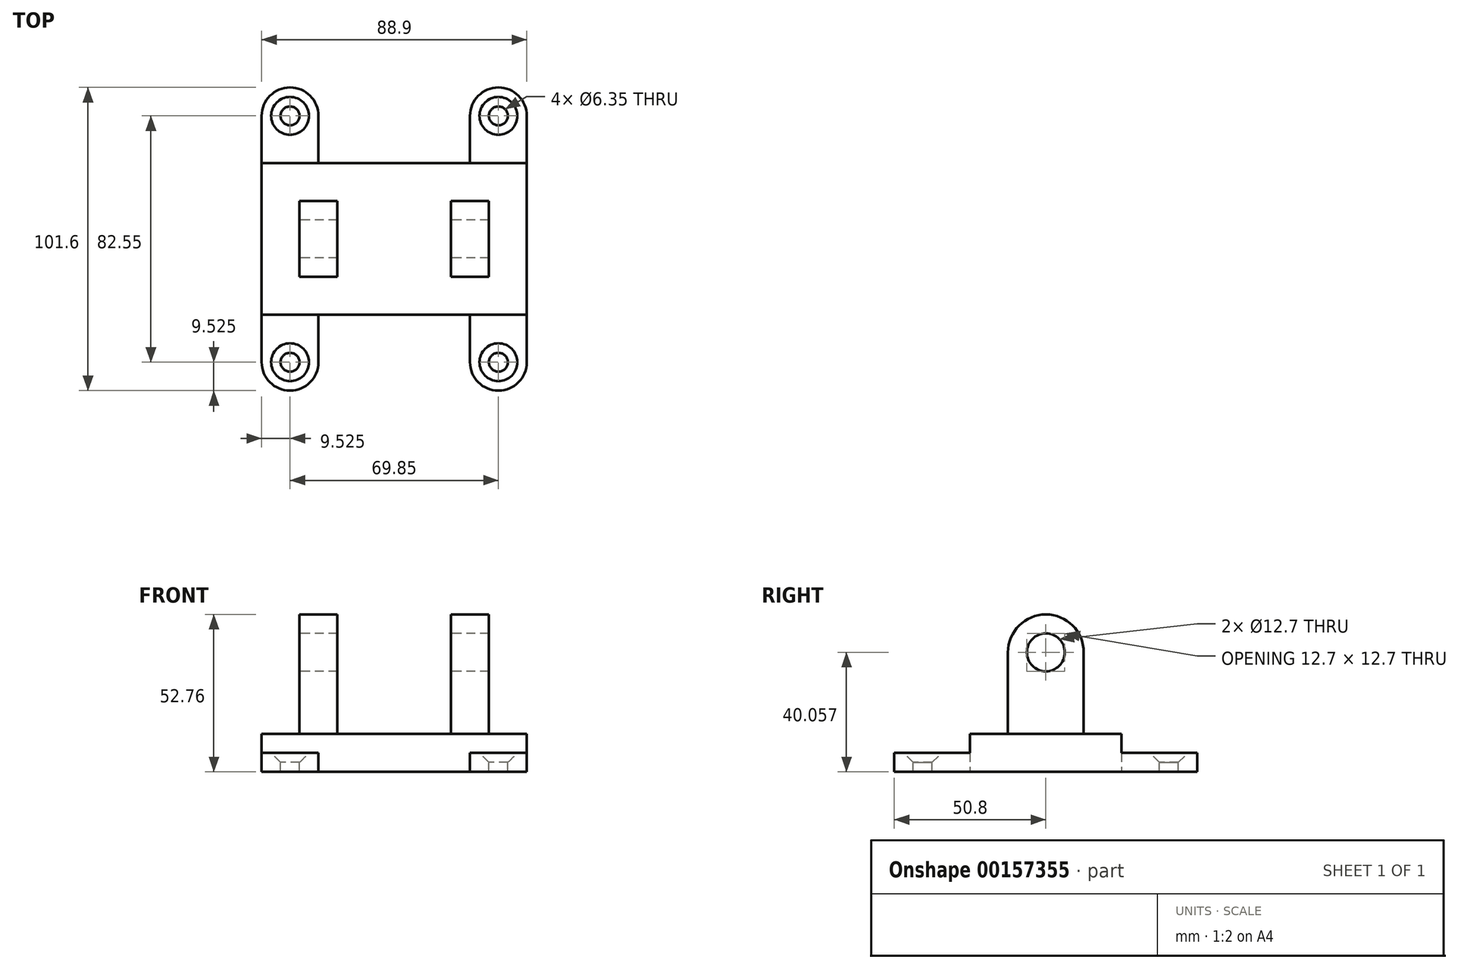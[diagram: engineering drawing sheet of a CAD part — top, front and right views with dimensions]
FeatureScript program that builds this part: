
annotation { "Feature Type Name" : "Feature", "Feature Type Description" : "" }
export const myFeature = defineFeature(function(context is Context, id is Id, definition is map)
    precondition{}
    {
        {
            var Q0;
            Q0=qCreatedBy(makeId("Front.planeOp"),FACE);
            var sketch = newSketch(context, id + "F0", { "sketchPlane" : qUnion([Q0])});
            skLineSegment(sketch, "E0.bottom", {"start": v(0, 0) * mm, "end": v(88.9, 0) * mm});
            skLineSegment(sketch, "E0.top", {"start": v(0, 12.7) * mm, "end": v(88.9, 12.7) * mm});
            skLineSegment(sketch, "E0.left", {"start": v(0, 0) * mm, "end": v(0, 12.7) * mm});
            skLineSegment(sketch, "E0.right", {"start": v(88.9, 0) * mm, "end": v(88.9, 12.7) * mm});
            skSolve(sketch);
        }
        {
            var Q0;
            Q0 = qSketchRegion(id + "F0", true);
            extrude(context, id + "F1", {"entities" : qUnion([Q0]), "depth" : 50.8 * mm});
        }
        {
            var Q0;
            Q0=qCreatedBy(makeId("Top.planeOp"),FACE);
            var sketch = newSketch(context, id + "F2", { "sketchPlane" : qUnion([Q0])});
            skLineSegment(sketch, "E1", {"start": v(0, 0) * mm, "end": v(0, 15.88) * mm});
            skLineSegment(sketch, "E2", {"start": v(0, 15.88) * mm, "end": v(19.05, 15.88) * mm});
            skLineSegment(sketch, "E3", {"start": v(19.05, 15.88) * mm, "end": v(19.05, 0) * mm});
            skLineSegment(sketch, "E4", {"start": v(19.05, 0) * mm, "end": v(69.85, 0) * mm});
            skLineSegment(sketch, "E5", {"start": v(69.85, 0) * mm, "end": v(69.85, 15.88) * mm});
            skLineSegment(sketch, "E6", {"start": v(69.85, 15.88) * mm, "end": v(88.9, 15.88) * mm});
            skLineSegment(sketch, "E7", {"start": v(88.9, 15.88) * mm, "end": v(88.9, 0) * mm});
            skLineSegment(sketch, "E8", {"start": v(0, 0) * mm, "end": v(0, -66.67) * mm});
            skLineSegment(sketch, "E9", {"start": v(0, -66.67) * mm, "end": v(19.05, -66.67) * mm});
            skLineSegment(sketch, "E10", {"start": v(19.05, -66.67) * mm, "end": v(19.05, -50.8) * mm});
            skLineSegment(sketch, "E11", {"start": v(19.05, -50.8) * mm, "end": v(69.85, -50.8) * mm});
            skLineSegment(sketch, "E12", {"start": v(69.85, -50.8) * mm, "end": v(69.85, -66.67) * mm});
            skLineSegment(sketch, "E13", {"start": v(69.85, -66.67) * mm, "end": v(88.9, -66.67) * mm});
            skLineSegment(sketch, "E14", {"start": v(88.9, -66.67) * mm, "end": v(88.9, -50.8) * mm});
            skArc(sketch, "E15", {"start": v(19.05, 15.88) * mm, "mid": v(9.53, 25.4) * mm, "end": v(0, 15.88) * mm});
            skArc(sketch, "E16", {"start": v(88.9, 15.88) * mm, "mid": v(79.38, 25.4) * mm, "end": v(69.85, 15.88) * mm});
            skArc(sketch, "E17", {"start": v(0, -66.67) * mm, "mid": v(9.53, -76.2) * mm, "end": v(19.05, -66.67) * mm});
            skArc(sketch, "E18", {"start": v(69.85, -66.67) * mm, "mid": v(79.38, -76.2) * mm, "end": v(88.9, -66.67) * mm});
            skLineSegment(sketch, "E19", {"start": v(0, -50.8) * mm, "end": v(19.05, -50.8) * mm});
            skLineSegment(sketch, "E20", {"start": v(69.85, -50.8) * mm, "end": v(88.9, -50.8) * mm});
            skLineSegment(sketch, "E21", {"start": v(69.85, 0) * mm, "end": v(88.9, 0) * mm});
            skLineSegment(sketch, "E22", {"start": v(19.05, 0) * mm, "end": v(0, 0) * mm});
            skCircle(sketch, "E23", {"center": v(79.38, 15.87) * mm, "radius": 3.18 * mm, "construction": true});
            skCircle(sketch, "E24", {"center": v(79.38, -66.67) * mm, "radius": 3.18 * mm, "construction": true});
            skCircle(sketch, "E25", {"center": v(9.53, -66.67) * mm, "radius": 3.18 * mm, "construction": true});
            skCircle(sketch, "E26", {"center": v(9.53, 15.88) * mm, "radius": 3.18 * mm, "construction": true});
            skSolve(sketch);
        }
        {
            var Q0;
            Q0 = qSketchRegion(id + "F2", true);
            extrude(context, id + "F3", {"entities" : qUnion([Q0]), "operationType" : NewBodyOperationType.ADD, "depth" : 6.35 * mm});
        }
        {
            var Q0;
            Q0=qCreatedBy(makeId("Right.planeOp"),FACE);
            var sketch = newSketch(context, id + "F4", { "sketchPlane" : qUnion([Q0])});
            skLineSegment(sketch, "E27.bottom", {"start": v(0, 0) * mm, "end": v(-50.8, 0) * mm});
            skLineSegment(sketch, "E27.top", {"start": v(0, 12.57) * mm, "end": v(-50.8, 12.57) * mm});
            skLineSegment(sketch, "E27.left", {"start": v(0, 0) * mm, "end": v(0, 12.57) * mm});
            skLineSegment(sketch, "E27.right", {"start": v(-50.8, 0) * mm, "end": v(-50.8, 12.57) * mm});
            skLineSegment(sketch, "E28", {"start": v(-38.1, 12.57) * mm, "end": v(-38.1, 40.06) * mm});
            skLineSegment(sketch, "E29", {"start": v(-38.1, 40.06) * mm, "end": v(-12.7, 40.06) * mm, "construction": true});
            skLineSegment(sketch, "E30", {"start": v(-12.7, 40.06) * mm, "end": v(-12.7, 12.57) * mm});
            skArc(sketch, "E31", {"start": v(-12.7, 40.06) * mm, "mid": v(-25.4, 52.76) * mm, "end": v(-38.1, 40.06) * mm});
            skCircle(sketch, "E32", {"center": v(-25.4, 40.06) * mm, "radius": 6.35 * mm});
            skSolve(sketch);
        }
        {
            var Q0;
            Q0 = qSketchRegion(id + "F4", true);
            extrude(context, id + "F5", {"entities" : qUnion([Q0]), "operationType" : NewBodyOperationType.ADD, "depth" : 76.2 * mm, "hasSecondDirection" : true, "secondDirectionOppositeDirection" : false, "secondDirectionDepth" : 12.7 * mm});
        }
        {
            var Q0;
            Q0=qCreatedBy(makeId("Front.planeOp"),FACE);
            var sketch = newSketch(context, id + "F6", { "sketchPlane" : qUnion([Q0])});
            skLineSegment(sketch, "E33.bottom", {"start": v(25.4, 12.7) * mm, "end": v(63.5, 12.7) * mm});
            skLineSegment(sketch, "E33.top", {"start": v(25.4, 57.15) * mm, "end": v(63.5, 57.15) * mm});
            skLineSegment(sketch, "E33.left", {"start": v(25.4, 12.7) * mm, "end": v(25.4, 57.15) * mm});
            skLineSegment(sketch, "E33.right", {"start": v(63.5, 12.7) * mm, "end": v(63.5, 57.15) * mm});
            skSolve(sketch);
        }
        {
            var Q0;
            Q0 = qSketchRegion(id + "F6", true);
            extrude(context, id + "F7", {"entities" : qUnion([Q0]), "operationType" : NewBodyOperationType.REMOVE, "depth" : 50.8 * mm});
        }
        {
            var Q0;
            Q0=makeQuery(id+"F3.opExtrude","CAP_FACE",FACE,{"disambiguationData":[OSD([sQuery(id+"F2.wireOp",EDGE,"E8"),sQuery(id+"F2.wireOp",EDGE,"E10"),sQuery(id+"F2.wireOp",EDGE,"E17"),sQuery(id+"F2.wireOp",EDGE,"E19")])],"isStart":false});
            var sketch = newSketch(context, id + "F8", { "sketchPlane" : qUnion([Q0])});
            skPoint(sketch, "E34", {"position": v(9.53, -66.67) * mm});
            skPoint(sketch, "E35", {"position": v(79.38, -66.67) * mm});
            skPoint(sketch, "E36", {"position": v(9.53, 15.88) * mm});
            skPoint(sketch, "E37", {"position": v(79.38, 15.87) * mm});
            skSolve(sketch);
        }
        {
            var Q0;
            Q0=sQuery(id+"F8.wireOp",VERTEX,"E34");
            var Q1;
            Q1=sQuery(id+"F8.wireOp",VERTEX,"E35");
            var Q2;
            Q2=sQuery(id+"F8.wireOp",VERTEX,"E36");
            var Q3;
            Q3=sQuery(id+"F8.wireOp",VERTEX,"E37");
            var Q4;
            Q4=makeQuery(id+"F1.opExtrude","SWEPT_BODY",BODY,{"disambiguationData":[OSD([sQuery(id+"F0.wireOp",EDGE,"E0.bottom"),sQuery(id+"F0.wireOp",EDGE,"E0.top"),sQuery(id+"F0.wireOp",EDGE,"E0.left"),sQuery(id+"F0.wireOp",EDGE,"E0.right")])]});
            hole(context, id + "F9", {"style" : HoleStyle.C_SINK, "endStyle" : HoleEndStyle.THROUGH, "holeDiameter" : 6.35 * mm, "cSinkDiameter" : 12.7 * mm, "cSinkAngle" : 90 * degree, "locations" : qUnion([Q0, Q1, Q2, Q3]), "scope" : qUnion([Q4]), "isTappedThrough" : true});
        }
    });
